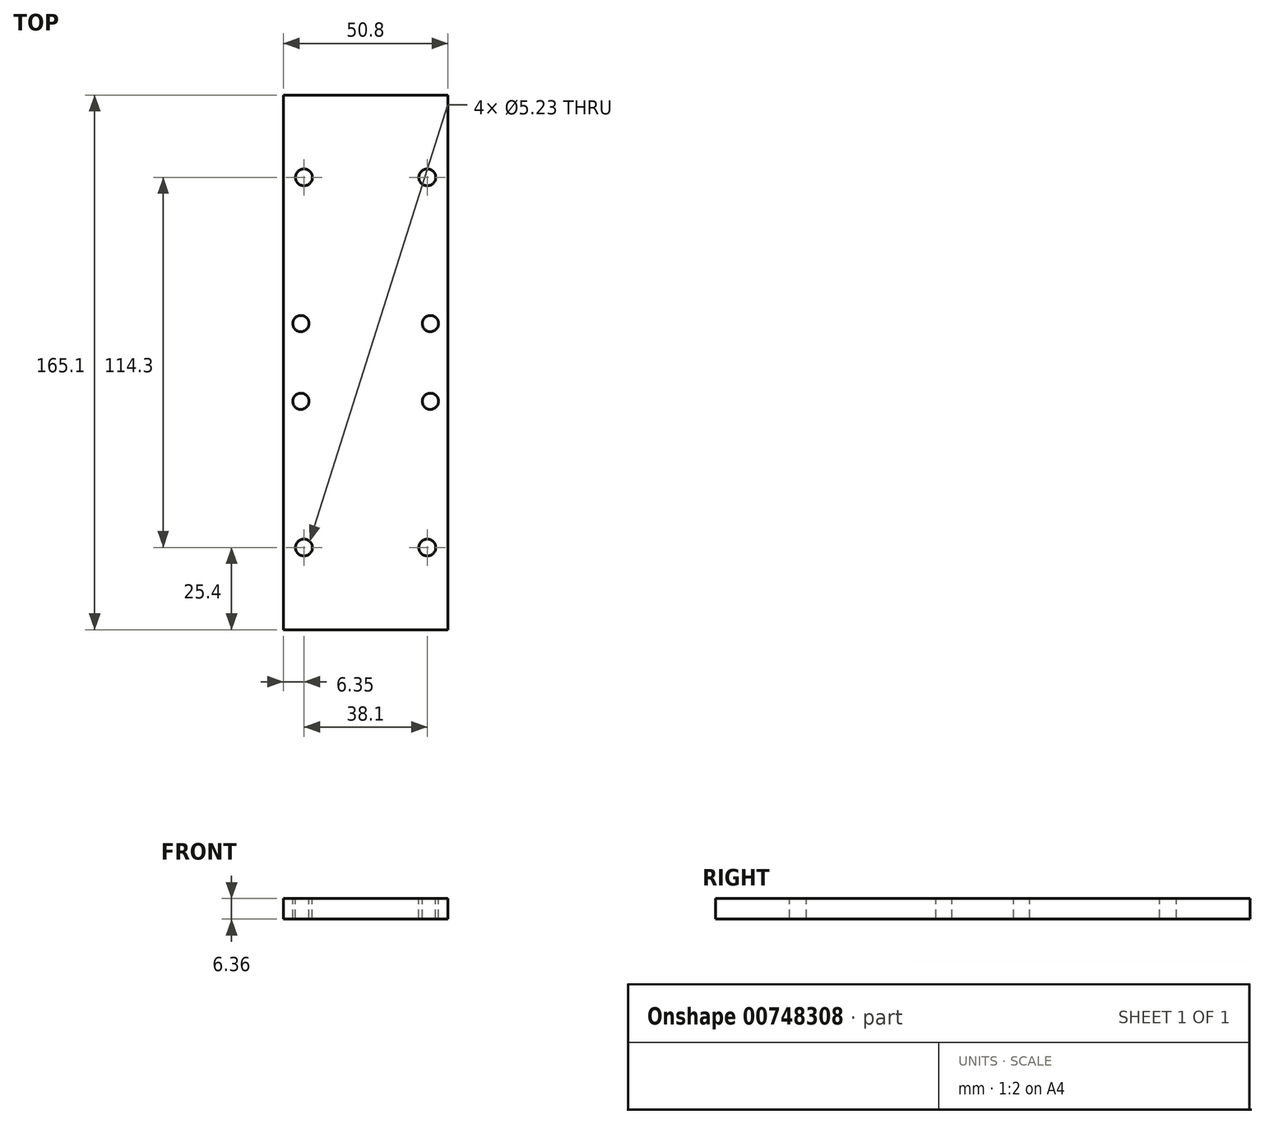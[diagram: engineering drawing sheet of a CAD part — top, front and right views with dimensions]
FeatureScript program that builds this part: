
annotation { "Feature Type Name" : "Feature", "Feature Type Description" : "" }
export const myFeature = defineFeature(function(context is Context, id is Id, definition is map)
    precondition{}
    {
        {
            var Q0;
            Q0=qCreatedBy(makeId("Front.planeOp"),FACE);
            var sketch = newSketch(context, id + "F0", { "sketchPlane" : qUnion([Q0])});
            skLineSegment(sketch, "E0.bottom", {"start": v(25.4, 3.18) * mm, "end": v(-25.4, 3.18) * mm});
            skLineSegment(sketch, "E0.top", {"start": v(25.4, -3.17) * mm, "end": v(-25.4, -3.17) * mm});
            skLineSegment(sketch, "E0.left", {"start": v(25.4, 3.18) * mm, "end": v(25.4, -3.17) * mm});
            skLineSegment(sketch, "E0.right", {"start": v(-25.4, 3.18) * mm, "end": v(-25.4, -3.17) * mm});
            skPoint(sketch, "E0.middle", {"position": v(0, 0) * mm});
            skSolve(sketch);
        }
        {
            var Q0;
            Q0=qSketchRegion(id+"F0",true);
            extrude(context, id + "F1", {"entities" : qUnion([Q0]), "depth" : 165.1 * mm, "offsetDistance" : 25.4 * mm});
        }
        {
            var Q0;
            Q0=makeQuery(id+"F1.opExtrude","SWEPT_FACE",FACE,{"disambiguationData":[OSD([sQuery(id+"F0.wireOp",EDGE,"E0.bottom")])]});
            var sketch = newSketch(context, id + "F2", { "sketchPlane" : qUnion([Q0])});
            skLineSegment(sketch, "E1", {"start": v(-25.4, -25.4) * mm, "end": v(25.4, -25.4) * mm, "construction": true});
            skLineSegment(sketch, "E2", {"start": v(0, -165.1) * mm, "end": v(0, 0) * mm, "construction": true});
            skLineSegment(sketch, "E3.bottom", {"start": v(20, -70.55) * mm, "end": v(-20, -70.55) * mm, "construction": true});
            skLineSegment(sketch, "E3.top", {"start": v(20, -94.55) * mm, "end": v(-20, -94.55) * mm, "construction": true});
            skLineSegment(sketch, "E3.left", {"start": v(20, -70.55) * mm, "end": v(20, -94.55) * mm, "construction": true});
            skLineSegment(sketch, "E3.right", {"start": v(-20, -70.55) * mm, "end": v(-20, -94.55) * mm, "construction": true});
            skPoint(sketch, "E3.middle", {"position": v(0, -82.55) * mm});
            skLineSegment(sketch, "E4", {"start": v(-25.4, -139.7) * mm, "end": v(25.4, -139.7) * mm, "construction": true});
            skCircle(sketch, "E5", {"center": v(-20, -94.55) * mm, "radius": 2.5 * mm});
            skCircle(sketch, "E6", {"center": v(20, -94.55) * mm, "radius": 2.5 * mm});
            skCircle(sketch, "E7", {"center": v(20, -70.55) * mm, "radius": 2.5 * mm});
            skCircle(sketch, "E8", {"center": v(-20, -70.55) * mm, "radius": 2.5 * mm});
            skLineSegment(sketch, "E9.0", {"start": v(19.05, -165.1) * mm, "end": v(19.05, 0) * mm, "construction": true});
            skLineSegment(sketch, "E10.0", {"start": v(-19.05, -165.1) * mm, "end": v(-19.05, 0) * mm, "construction": true});
            skCircle(sketch, "E11", {"center": v(-19.05, -139.7) * mm, "radius": 2.62 * mm});
            skCircle(sketch, "E12", {"center": v(19.05, -139.7) * mm, "radius": 2.62 * mm});
            skCircle(sketch, "E13", {"center": v(-19.05, -25.4) * mm, "radius": 2.62 * mm});
            skCircle(sketch, "E14", {"center": v(19.05, -25.4) * mm, "radius": 2.62 * mm});
            skLineSegment(sketch, "E15", {"start": v(-25.4, -82.55) * mm, "end": v(25.4, -82.55) * mm, "construction": true});
            skSolve(sketch);
        }
        {
            var Q0;
            Q0=qSketchRegion(id+"F2",true);
            extrude(context, id + "F3", {"entities" : qUnion([Q0]), "operationType" : NewBodyOperationType.REMOVE, "endBound" : BoundingType.THROUGH_ALL, "oppositeDirection" : true, "depth" : 25.4 * mm, "offsetDistance" : 25.4 * mm});
        }
    });
